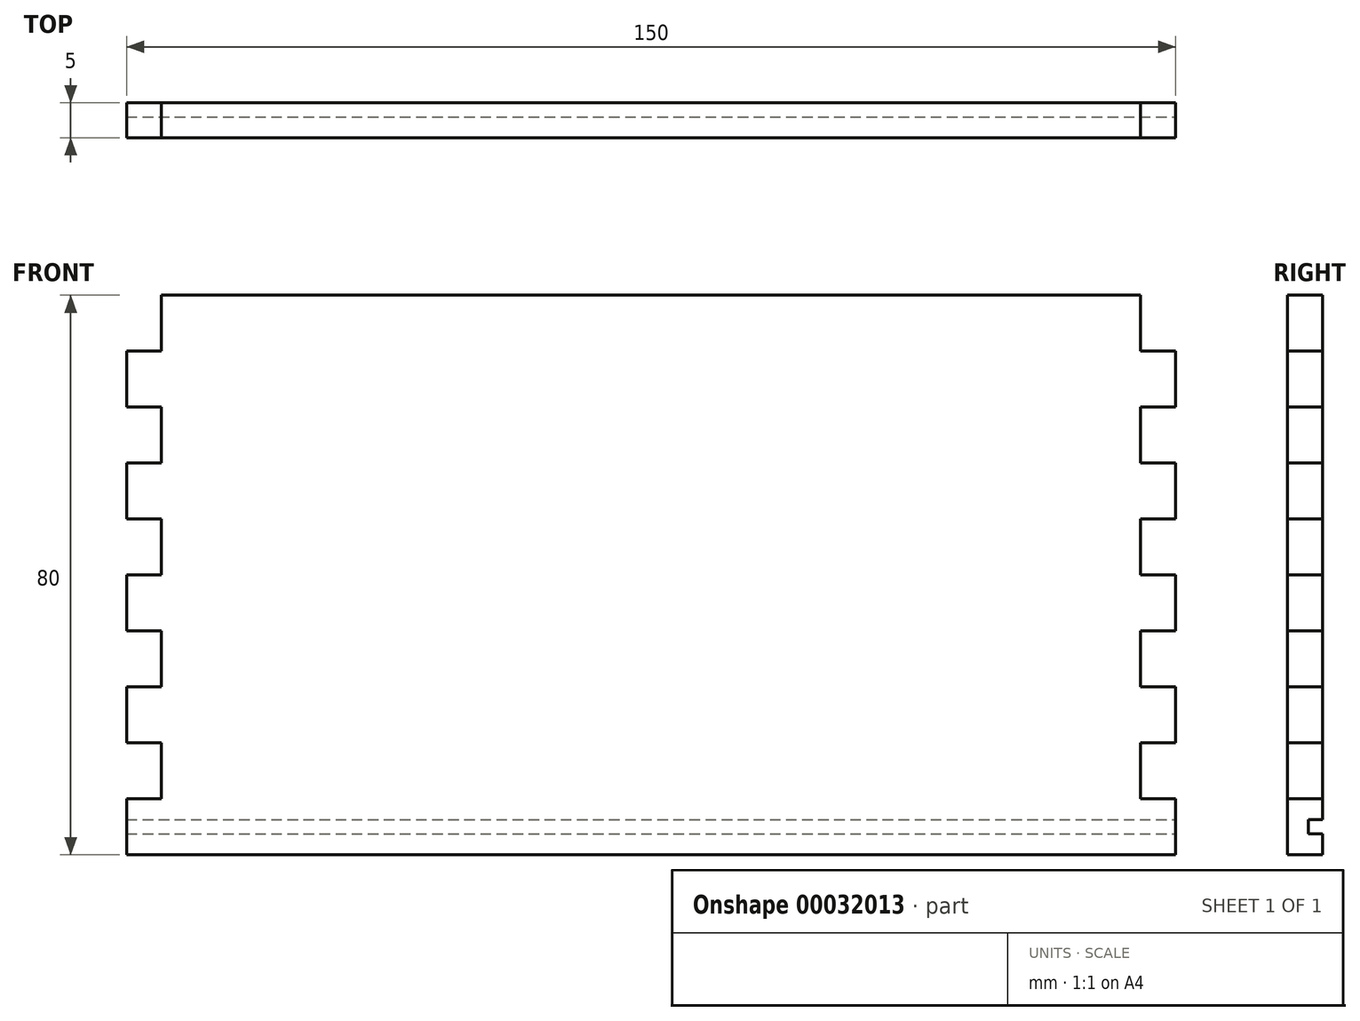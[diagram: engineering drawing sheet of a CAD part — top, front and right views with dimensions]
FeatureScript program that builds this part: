
annotation { "Feature Type Name" : "Feature", "Feature Type Description" : "" }
export const myFeature = defineFeature(function(context is Context, id is Id, definition is map)
    precondition{}
    {
        {
            assignVariable(context, id + "F0", {"name" : "ep", "anyValue" : 5});
        }
        {
            var Q0;
            Q0=qCreatedBy(makeId("Front.planeOp"),FACE);
            var sketch = newSketch(context, id + "F1", { "sketchPlane" : qUnion([Q0])});
            skLineSegment(sketch, "E0", {"start": v(70, 0) * mm, "end": v(70, -8) * mm});
            skLineSegment(sketch, "E1", {"start": v(70, -8) * mm, "end": v(75, -8) * mm});
            skLineSegment(sketch, "E2", {"start": v(75, -8) * mm, "end": v(75, -16) * mm});
            skLineSegment(sketch, "E3", {"start": v(75, -16) * mm, "end": v(70, -16) * mm});
            skLineSegment(sketch, "E4", {"start": v(70, -16) * mm, "end": v(70, -24) * mm});
            skLineSegment(sketch, "E5", {"start": v(70, -24) * mm, "end": v(75, -24) * mm});
            skLineSegment(sketch, "E6", {"start": v(75, -24) * mm, "end": v(75, -32) * mm});
            skLineSegment(sketch, "E7", {"start": v(75, -32) * mm, "end": v(70, -32) * mm});
            skLineSegment(sketch, "E8", {"start": v(70, -32) * mm, "end": v(70, -40) * mm});
            skLineSegment(sketch, "E9", {"start": v(70, -40) * mm, "end": v(75, -40) * mm});
            skLineSegment(sketch, "E10", {"start": v(75, -40) * mm, "end": v(75, -48) * mm});
            skLineSegment(sketch, "E11", {"start": v(75, -48) * mm, "end": v(70, -48) * mm});
            skLineSegment(sketch, "E12", {"start": v(70, -48) * mm, "end": v(70, -56) * mm});
            skLineSegment(sketch, "E13", {"start": v(70, -56) * mm, "end": v(75, -56) * mm});
            skLineSegment(sketch, "E14", {"start": v(75, -56) * mm, "end": v(75, -64) * mm});
            skLineSegment(sketch, "E15", {"start": v(75, -64) * mm, "end": v(70, -64) * mm});
            skLineSegment(sketch, "E16", {"start": v(70, -64) * mm, "end": v(70, -72) * mm});
            skLineSegment(sketch, "E17", {"start": v(70, -72) * mm, "end": v(75, -72) * mm});
            skLineSegment(sketch, "E18", {"start": v(75, -72) * mm, "end": v(75, -80) * mm});
            skLineSegment(sketch, "E19.MirrorCS", {"start": v(-70, -56) * mm, "end": v(-75, -56) * mm});
            skLineSegment(sketch, "E20.MirrorCS", {"start": v(-75, -48) * mm, "end": v(-70, -48) * mm});
            skLineSegment(sketch, "E21.MirrorCS", {"start": v(-70, -8) * mm, "end": v(-75, -8) * mm});
            skLineSegment(sketch, "E22.MirrorCS", {"start": v(-75, -64) * mm, "end": v(-70, -64) * mm});
            skLineSegment(sketch, "E23.MirrorCS", {"start": v(-75, -16) * mm, "end": v(-70, -16) * mm});
            skLineSegment(sketch, "E24.MirrorCS", {"start": v(-70, -24) * mm, "end": v(-75, -24) * mm});
            skLineSegment(sketch, "E25.MirrorCS", {"start": v(-70, -40) * mm, "end": v(-75, -40) * mm});
            skLineSegment(sketch, "E26.MirrorCS", {"start": v(-75, -32) * mm, "end": v(-70, -32) * mm});
            skLineSegment(sketch, "E27.MirrorCS", {"start": v(-70, -72) * mm, "end": v(-75, -72) * mm});
            skLineSegment(sketch, "E28.MirrorCS", {"start": v(-70, -48) * mm, "end": v(-70, -56) * mm});
            skLineSegment(sketch, "E29.MirrorCS", {"start": v(70, 0) * mm, "end": v(-70, 0) * mm});
            skLineSegment(sketch, "E30.MirrorCS", {"start": v(-75, -56) * mm, "end": v(-75, -64) * mm});
            skLineSegment(sketch, "E31.MirrorCS", {"start": v(-70, 0) * mm, "end": v(-70, -8) * mm});
            skLineSegment(sketch, "E32.MirrorCS", {"start": v(-70, -64) * mm, "end": v(-70, -72) * mm});
            skLineSegment(sketch, "E33.MirrorCS", {"start": v(-75, -8) * mm, "end": v(-75, -16) * mm});
            skLineSegment(sketch, "E34.MirrorCS", {"start": v(-75, -72) * mm, "end": v(-75, -80) * mm});
            skLineSegment(sketch, "E35.MirrorCS", {"start": v(-70, -32) * mm, "end": v(-70, -40) * mm});
            skLineSegment(sketch, "E36.MirrorCS", {"start": v(-70, -16) * mm, "end": v(-70, -24) * mm});
            skLineSegment(sketch, "E37.MirrorCS", {"start": v(-75, -40) * mm, "end": v(-75, -48) * mm});
            skLineSegment(sketch, "E38.MirrorCS", {"start": v(-75, -24) * mm, "end": v(-75, -32) * mm});
            skLineSegment(sketch, "E39.MirrorCS", {"start": v(-75, -80) * mm, "end": v(75, -80) * mm});
            skSolve(sketch);
        }
        {
            var Q0;
            Q0=makeQuery(id+"F1.imprint","IMPRINT",FACE,{"disambiguationData":[TD([[makeQuery(id+"F1.imprint","IMPRINT",EDGE,{"derivedFrom":sQuery(id+"F1.wireOp",EDGE,"4d24d0cb-3a33-4ae4-9eac-0c108ab8329b")}),-1.0]])]});
            var Q1;
            Q1=makeQuery(id+"F1.imprint","IMPRINT",FACE,{"disambiguationData":[TD([[makeQuery(id+"F1.imprint","IMPRINT",EDGE,{"derivedFrom":sQuery(id+"F1.wireOp",EDGE,"E0")}),-1.0]])]});
            extrude(context, id + "F2", {"entities" : qUnion([Q0, Q1]), "depth" : (getVariable(context, 'ep')) * mm});
        }
        {
            var Q0;
            Q0=makeQuery(id+"F2.opExtrude","SWEPT_FACE",FACE,{"disambiguationData":[OSD([sQuery(id+"F1.wireOp",EDGE,"E18")])]});
            var sketch = newSketch(context, id + "F3", { "sketchPlane" : qUnion([Q0])});
            skLineSegment(sketch, "E40", {"start": v(0, -75) * mm, "end": v(-2, -75) * mm});
            skLineSegment(sketch, "E41", {"start": v(-2, -75) * mm, "end": v(-2, -77) * mm});
            skLineSegment(sketch, "E42", {"start": v(-2, -77) * mm, "end": v(0, -77) * mm});
            skLineSegment(sketch, "E43", {"start": v(0, -77) * mm, "end": v(0, -75) * mm});
            skSolve(sketch);
        }
        {
            var Q0;
            Q0=makeQuery(id+"F3.imprint","IMPRINT",FACE,{"disambiguationData":[TD([[makeQuery(id+"F3.imprint","IMPRINT",EDGE,{"derivedFrom":sQuery(id+"F3.wireOp",EDGE,"E40")}),1.0]])]});
            extrude(context, id + "F4", {"entities" : qUnion([Q0]), "operationType" : NewBodyOperationType.REMOVE, "endBound" : BoundingType.THROUGH_ALL, "oppositeDirection" : true, "depth" : 25 * mm});
        }
    });
